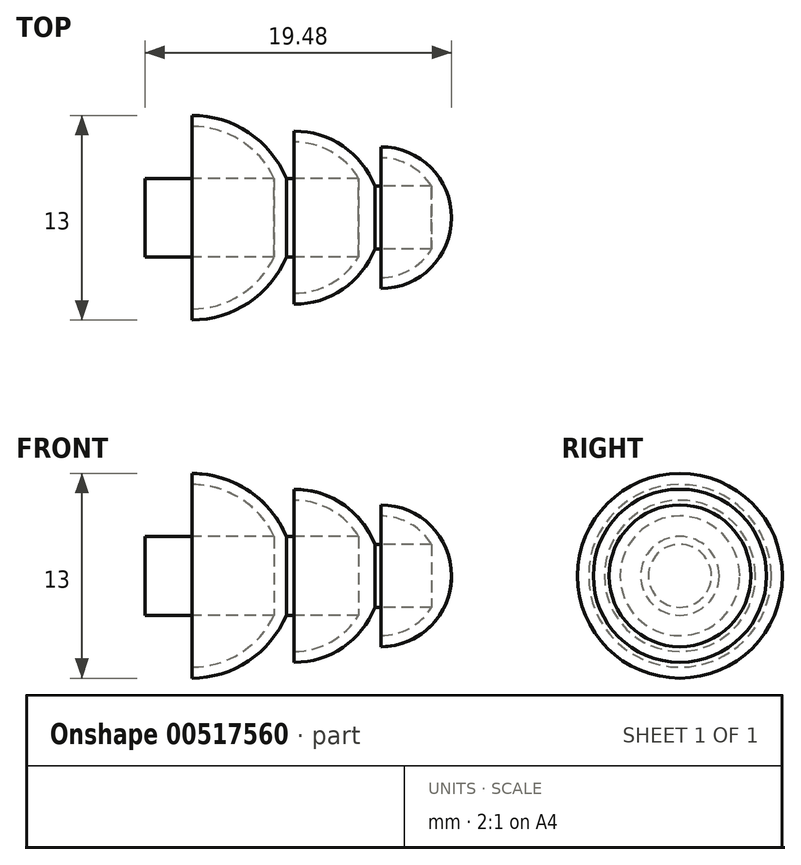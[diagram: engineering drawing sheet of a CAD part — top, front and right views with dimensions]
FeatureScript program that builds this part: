
annotation { "Feature Type Name" : "Feature", "Feature Type Description" : "" }
export const myFeature = defineFeature(function(context is Context, id is Id, definition is map)
    precondition{}
    {
        {
            var Q0;
            Q0=qCreatedBy(makeId("Front.planeOp"),FACE);
            var sketch = newSketch(context, id + "F0", { "sketchPlane" : qUnion([Q0])});
            skLineSegment(sketch, "E0", {"start": v(6.8, 2.5) * mm, "end": v(2.2, 2.5) * mm});
            skLineSegment(sketch, "E1", {"start": v(-6.78, 2.5) * mm, "end": v(-6.78, 0) * mm});
            skLineSegment(sketch, "E2", {"start": v(7.82, 2) * mm, "end": v(11.43, 2) * mm});
            skLineSegment(sketch, "E3", {"start": v(-6.78, 0) * mm, "end": v(12.7, 0) * mm});
            skArc(sketch, "E4", {"start": v(12.7, 0) * mm, "mid": v(11.38, 3.18) * mm, "end": v(8.2, 4.5) * mm});
            skArc(sketch, "E5.0", {"start": v(11.43, 2) * mm, "mid": v(10.05, 3.32) * mm, "end": v(8.2, 3.8) * mm});
            skLineSegment(sketch, "E6", {"start": v(8.2, 4.5) * mm, "end": v(8.2, 3.8) * mm});
            skPoint(sketch, "E7.orphan", {"position": v(12.7, 2) * mm});
            skArc(sketch, "E8", {"start": v(7.82, 2) * mm, "mid": v(5.8, 4.54) * mm, "end": v(2.7, 5.5) * mm});
            skPoint(sketch, "E9.orphan", {"position": v(7.7, 2) * mm});
            skArc(sketch, "E10.0", {"start": v(6.8, 2.5) * mm, "mid": v(5.05, 4.19) * mm, "end": v(2.7, 4.8) * mm});
            skLineSegment(sketch, "E11", {"start": v(2.7, 5.5) * mm, "end": v(2.7, 4.8) * mm});
            skArc(sketch, "E12", {"start": v(2.2, 2.5) * mm, "mid": v(-0.2, 5.4) * mm, "end": v(-3.8, 6.5) * mm});
            skArc(sketch, "E13.0", {"start": v(1.43, 2.5) * mm, "mid": v(-0.7, 4.9) * mm, "end": v(-3.8, 5.8) * mm});
            skLineSegment(sketch, "E14", {"start": v(-3.8, 6.5) * mm, "end": v(-3.8, 5.8) * mm});
            skLineSegment(sketch, "E15.trimOffspring", {"start": v(1.43, 2.5) * mm, "end": v(-6.78, 2.5) * mm});
            skSolve(sketch);
        }
        {
            var Q0;
            Q0 = qSketchRegion(id + "F0", true);
            var Q1;
            Q1=sQuery(id+"F0.wireOp",EDGE,"E3");
            revolve(context, id + "F1", {"entities" : qUnion([Q0]), "axis" : qUnion([Q1]), "revolveType" : RevolveType.FULL});
        }
    });
